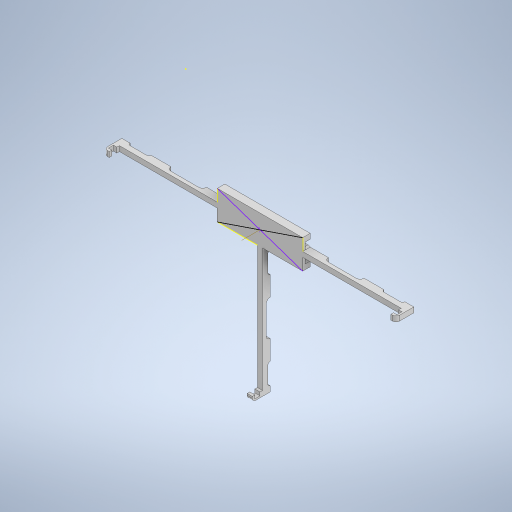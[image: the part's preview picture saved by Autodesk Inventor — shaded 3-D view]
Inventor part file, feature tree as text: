
AUTODESK INVENTOR PART (.ipt)
format: ipt  version: 2023 (Build 270158000, 158)  size: 489,472 bytes
history: native  units: mm
features: sketch x12, extrude x11, projected_geometry x8, other x6, fillet x2, pattern_circular x1
ambient origin geometry x8: Origin, YZ Plane, XZ Plane, XY Plane, X Axis, Y Axis, Z Axis, Center Point
bodies: Solide1 (feature_tree)
feature tree (40):
  extrude  "Extrusion1"  Depth=0.5mm
  extrude  "Extrusion2"  Depth=50.0mm
  extrude  "Extrusion3"  Depth=3.0mm
  extrude  "Extrusion4"  Depth=3.0mm
  sketch  "Esquisse5"
  extrude  "Extrusion5"  Depth=2.9mm TaperAngle=0.0deg
  extrude  "Extrusion6"  Depth=82.5mm
  extrude  "Extrusion7"  Depth=82.5mm
  extrude  "Extrusion8"  Depth=1.5mm
  extrude  "Extrusion9"  Depth=1.5mm
  fillet  "Congé1"  Radius=1.5mm
  extrude  "Extrusion10"  Depth=3.0mm
  sketch  "Esquisse11"
  other  "Axe de construction1"
  pattern_circular  "Réseau circulaire1"  [2 undecoded]
  extrude  "Extrusion11"  Depth=1.5mm TaperAngle=0.0deg
  fillet  "Congé2"  Radius=1.5mm
  sketch  "Esquisse1"
  other  "Référence1"
  other  "Référence2"
  sketch  "Esquisse2"
  sketch  "Esquisse3"
  sketch  "Esquisse4"
  projected_geometry  "Boucle projetée1"
  projected_geometry  "Boucle projetée2"
  projected_geometry  "Boucle projetée3"
  projected_geometry  "Boucle projetée4"
  projected_geometry  "Boucle projetée5"
  sketch  "Esquisse6"
  sketch  "Esquisse7"
  sketch  "Esquisse8"
  projected_geometry  "Boucle projetée6"
  sketch  "Esquisse9"
  sketch  "Esquisse10"
  sketch  "Esquisse12"
  projected_geometry  "Boucle projetée7"
  projected_geometry  "Boucle projetée8"
  other  "<userpath>\Desktop\PE-SM\3D\Ensemble.iam"
  other  "Ensemble.iam"
  other  "PE:1"
note: 2 required parameter values undecoded (feature->parameter linkage not recoverable at this tier; creation-order binding heuristic only, values carry confidence <= 0.55)
